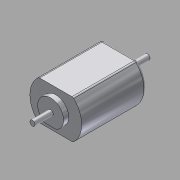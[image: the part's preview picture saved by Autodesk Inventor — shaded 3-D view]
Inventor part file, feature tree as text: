
AUTODESK INVENTOR PART (.ipt)
format: ipt  version: 2015 (Build 190159000, 159)  size: 135,680 bytes
history: native  units: in
note: dims shown in document units (in); Inventor stores cm internally (conversion verified against a paired STEP export)
features: sketch x5, other x3
ambient origin geometry x8: Origin, YZ Plane, XZ Plane, XY Plane, X Axis, Y Axis, Z Axis, Center Point
bodies: Solid1 (feature_tree)
feature tree (8):
  other  "motor.ipt"
  other  "Solid1::motor.ipt"
  other  "TaggingFeature1"
  sketch  "Sketch1"  dims[d0=0.3937in]
  sketch  "Sketch2"
  sketch  "Sketch3"
  sketch  "Sketch4"
  sketch  "Sketch5"
